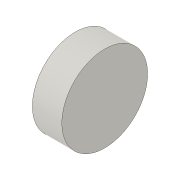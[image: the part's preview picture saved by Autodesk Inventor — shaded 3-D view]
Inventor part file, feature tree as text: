
AUTODESK INVENTOR PART (.ipt)
format: ipt  version: 2018 (Build 220112000, 112)  size: 75,264 bytes
history: native  units: in
note: dims shown in document units (in); Inventor stores cm internally (conversion verified against a paired STEP export)
features: extrude x1, sketch x1
ambient origin geometry x8: Origin, YZ Plane, XZ Plane, XY Plane, X Axis, Y Axis, Z Axis, Center Point
bodies: Solid1 (feature_tree)
feature tree (2):
  extrude  "Extrusion1"  Depth=5.5in TaperAngle=0.0deg
  sketch  "Sketch1"  dims[d0=16.0in d1=5.5in d2=0.0in]
